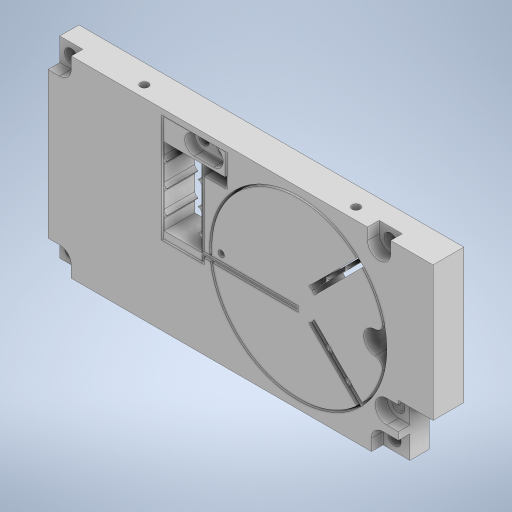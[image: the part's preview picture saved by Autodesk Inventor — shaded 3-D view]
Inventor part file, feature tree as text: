
AUTODESK INVENTOR PART (.ipt)
format: ipt  version: 2023 (Build 270158000, 158)  size: 734,208 bytes
history: native  units: mm
features: extrude x12, sketch x11, reference x5, other x5, fillet x1
ambient origin geometry x8: Origin, YZ Plane, XZ Plane, XY Plane, X Axis, Y Axis, Z Axis, Center Point
bodies: Solid1 (feature_tree)
feature tree (34):
  extrude  "Extrusion1"  Depth=8.0mm
  extrude  "Extrusion2"  Depth=9.0mm TaperAngle=0.0deg
  extrude  "Extrusion3"  Depth=40.0mm
  fillet  "Fillet1"  Radius=1.6mm
  extrude  "Extrusion4"  Depth=45.0mm
  extrude  "Extrusion5"  TaperAngle=45.0deg  [1 undecoded]
  extrude  "Extrusion6"  Depth=10.0mm
  extrude  "Extrusion7"  Depth=1.0mm
  extrude  "Extrusion8"  Depth=1.0mm
  extrude  "Extrusion9"  Depth=1.0mm
  extrude  "Extrusion10"  Depth=0.1mm
  extrude  "Extrusion11"  Depth=8.0mm TaperAngle=0.0deg
  extrude  "Extrusion12"  Depth=2.0mm
  sketch  "Sketch1"  dims[d0=8.0mm d1=0.0mm d2=9.0mm]
  reference  "Reference1"
  sketch  "Sketch2"  dims[d3=15.0mm d4=9.0mm d5=0.0mm]
  sketch  "Sketch3"  dims[d6=15.0mm d7=40.0mm d8=1.6mm]
  sketch  "Sketch4"  dims[d9=6.0mm d10=45.0mm]
  sketch  "Sketch5"  dims[d11=20.0mm d12=45.0deg]
  sketch  "Sketch8"  dims[d13=45.0deg d14=10.0mm]
  sketch  "Sketch10"  dims[d15=46.0mm d16=1.0mm]
  sketch  "Sketch11"  dims[d17=1.0mm d18=1.0mm]
  sketch  "Sketch12"  dims[d19=1.0mm d20=0.05mm]
  reference  "Reference6"
  reference  "Reference7"
  sketch  "Sketch13"  dims[d21=0.1mm d22=0.1mm]
  reference  "Reference10"
  reference  "Reference11"
  sketch  "Sketch14"  dims[d23=0.05mm d24=8.0mm d25=0.0mm d26=2.0mm d33=2.65mm d34=0.4mm d35=0.5mm d36=0.5mm d37=20.0mm d38=1.75mm d39=1.6mm d40=25.0mm d41=0.0mm d42=0.5mm d43=0.5mm d44=0.5mm d45=0.5mm d47=1.5mm d48=0.0mm d49=0.1mm d50=0.1mm d51=0.5mm d52=0.5mm d53=0.5mm d54=18.0mm d56=0.0mm d57=1.5mm d58=0.1mm d59=8.0mm d60=0.0mm d61=8.0mm d62=0.0mm d63=16.0mm d64=2.7mm d65=2.7mm d66=8.0mm d67=0.0mm d68=3.0mm d69=14.0mm d70=3.0mm d72=3.0mm d73=3.4mm d74=3.4mm d75=3.4mm d76=3.0mm d77=3.0mm d78=3.0mm d79=4.0mm d80=3.4mm d81=3.0mm d82=3.4mm d83=11.0mm d84=8.0mm d85=0.0mm d86=6.0mm d87=6.0mm d88=6.0mm d89=6.0mm d90=6.0mm d91=3.0mm d92=0.0mm d93=5.0mm d94=5.0mm d95=2.5mm d96=0.0mm d97=7.0mm d98=0.0mm d99=2.05mm d100=2.75mm d101=2.05mm d102=2.05mm d103=2.05mm d104=2.05mm d105=2.05mm d106=7.0mm d107=0.0mm d108=10.0mm d109=23.0mm d110=55.0mm d111=55.0mm d112=2.05mm d113=23.0mm d114=55.0mm d116=5.0mm d117=2.0mm d118=5.0mm d119=2.0mm d120=5.0mm d121=2.0mm d122=5.0mm d123=2.0mm d125=1.0mm d126=1.0mm d127=2.1mm d129=2.0mm d130=2.0mm d132=2.1mm d134=2.0mm d135=2.0mm d136=2.0mm d137=2.0mm d138=2.0mm d139=2.1mm d140=2.1mm d141=4.0mm d142=4.0mm d143=3.0mm d144=4.0mm d145=3.0mm d146=4.0mm d148=2.1mm d150=2.100022mm d151=2.699978mm d152=2.0mm d153=2.0mm d154=10.0mm d155=0.0mm d156=5.0mm d157=3.0mm]
  other  "<userpath>\ClawdDrive\Objet3D\IminaProbe\V3Roue\RoueV3.iam"
  other  "RoueV3.iam"
  other  "RoueV3PartB:1"
  other  "DifferentialLinearActuator:13"
  other  "DifferentialLinearActuator:14"
note: 1 required parameter value undecoded (feature->parameter linkage not recoverable at this tier; creation-order binding heuristic only, values carry confidence <= 0.55)
